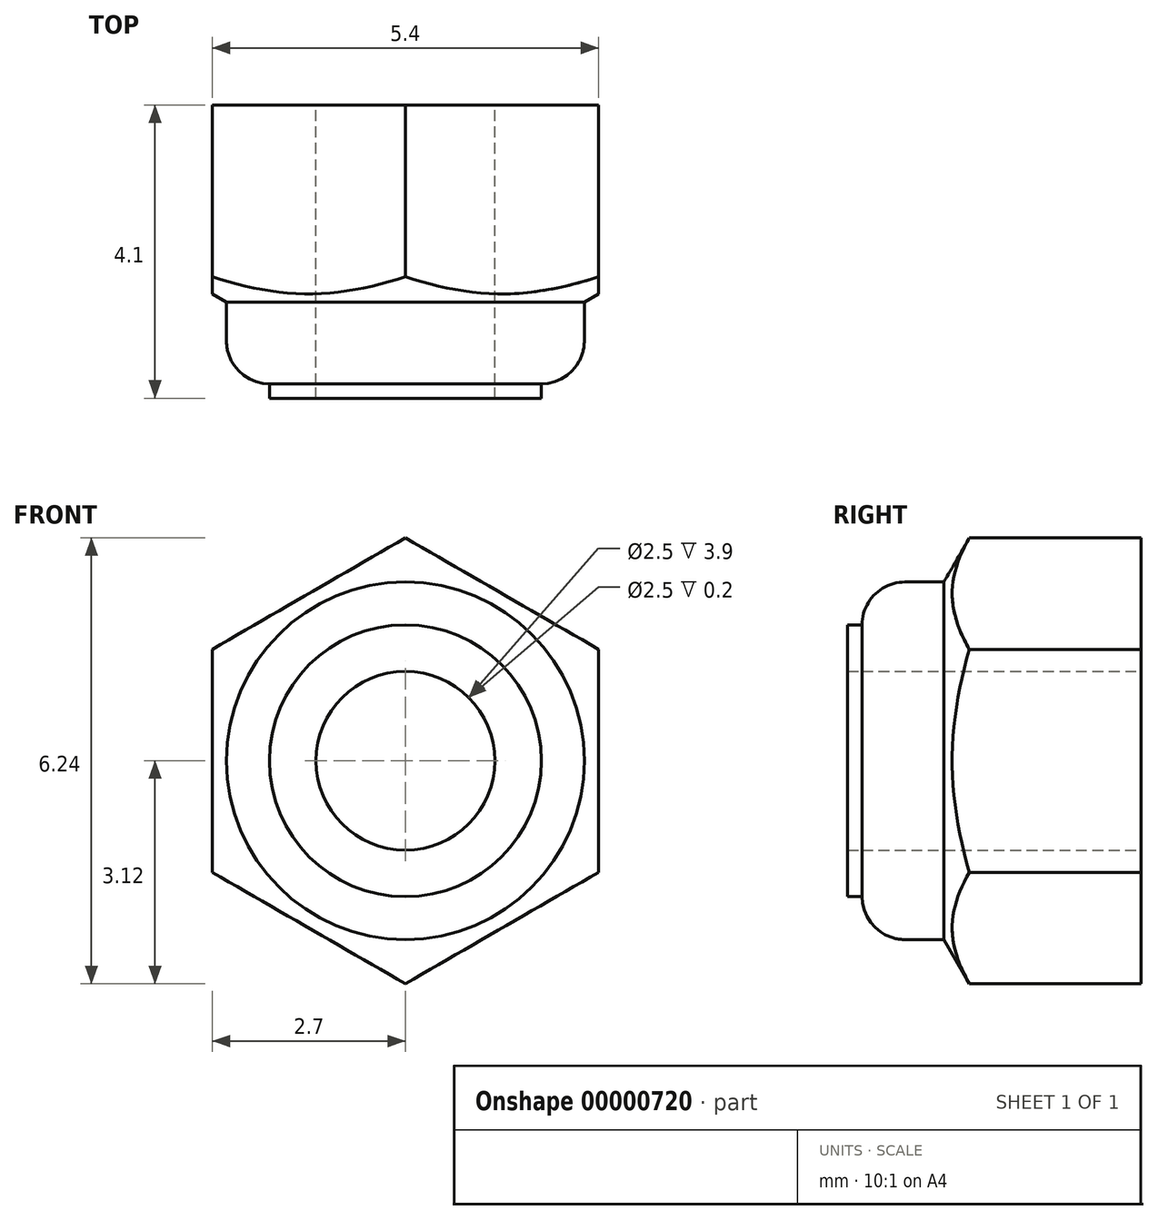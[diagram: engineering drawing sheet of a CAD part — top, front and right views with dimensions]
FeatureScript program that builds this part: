
annotation { "Feature Type Name" : "Feature", "Feature Type Description" : "" }
export const myFeature = defineFeature(function(context is Context, id is Id, definition is map)
    precondition{}
    {
        {
            var Q0;
            Q0=qCreatedBy(makeId("Front.planeOp"),FACE);
            var sketch = newSketch(context, id + "F0", { "sketchPlane" : qUnion([Q0])});
            skCircle(sketch, "E0.cCircle", {"center": v(0, 0) * mm, "radius": 2.7 * mm, "construction": true});
            skLineSegment(sketch, "E0.0", {"start": v(2.7, 1.56) * mm, "end": v(2.7, -1.56) * mm});
            skLineSegment(sketch, "E0.1", {"start": v(2.7, -1.56) * mm, "end": v(0, -3.12) * mm});
            skLineSegment(sketch, "E0.2", {"start": v(0, -3.12) * mm, "end": v(-2.7, -1.56) * mm});
            skLineSegment(sketch, "E0.3", {"start": v(-2.7, -1.56) * mm, "end": v(-2.7, 1.56) * mm});
            skLineSegment(sketch, "E0.4", {"start": v(-2.7, 1.56) * mm, "end": v(0, 3.12) * mm});
            skLineSegment(sketch, "E0.5", {"start": v(0, 3.12) * mm, "end": v(2.7, 1.56) * mm});
            skPoint(sketch, "E0.0.midPoint", {"position": v(2.7, 0) * mm});
            skSolve(sketch);
        }
        {
            var Q0;
            Q0=makeQuery(id+"F0.imprint","IMPRINT",FACE,{"disambiguationData":[TD([[makeQuery(id+"F0.imprint","IMPRINT",EDGE,{"derivedFrom":sQuery(id+"F0.wireOp",EDGE,"E0.0")}),-1.0]])]});
            extrude(context, id + "F1", {"entities" : qUnion([Q0]), "depth" : 3 * mm});
        }
        {
            var Q0;
            Q0=qCreatedBy(makeId("Right.planeOp"),FACE);
            var sketch = newSketch(context, id + "F2", { "sketchPlane" : qUnion([Q0])});
            skLineSegment(sketch, "E1", {"start": v(-2.4, 3.12) * mm, "end": v(-4.2, 0) * mm});
            skLineSegment(sketch, "E2", {"start": v(-4.2, 0) * mm, "end": v(-12.28, 0) * mm});
            skLineSegment(sketch, "E3", {"start": v(-12.28, 0) * mm, "end": v(-12.28, 3.12) * mm});
            skLineSegment(sketch, "E4", {"start": v(-2.4, 3.12) * mm, "end": v(-12.28, 3.12) * mm});
            skLineSegment(sketch, "E5", {"start": v(-4.2, 0) * mm, "end": v(3.9, 0) * mm, "construction": true});
            skSolve(sketch);
        }
        {
            var Q0;
            Q0=makeQuery(id+"F2.imprint","IMPRINT",FACE,{"disambiguationData":[TD([[makeQuery(id+"F2.imprint","IMPRINT",EDGE,{"derivedFrom":sQuery(id+"F2.wireOp",EDGE,"E1")}),-1.0]])]});
            var Q1;
            Q1=sQuery(id+"F2.wireOp",EDGE,"E5");
            revolve(context, id + "F3", {"operationType" : NewBodyOperationType.REMOVE, "entities" : qUnion([Q0]), "axis" : qUnion([Q1]), "revolveType" : RevolveType.FULL, "oppositeDirection" : true});
        }
        {
            var Q0;
            Q0=makeQuery(id+"F1.opExtrude","CAP_FACE",FACE,{"disambiguationData":[OSD([sQuery(id+"F0.wireOp",EDGE,"E0.0"),sQuery(id+"F0.wireOp",EDGE,"E0.1"),sQuery(id+"F0.wireOp",EDGE,"E0.2"),sQuery(id+"F0.wireOp",EDGE,"E0.3"),sQuery(id+"F0.wireOp",EDGE,"E0.4"),sQuery(id+"F0.wireOp",EDGE,"E0.5")])],"isStart":true});
            var sketch = newSketch(context, id + "F4", { "sketchPlane" : qUnion([Q0])});
            skCircle(sketch, "E6", {"center": v(0, 0) * mm, "radius": 2.5 * mm});
            skSolve(sketch);
        }
        {
            var Q0;
            Q0=makeQuery(id+"F4.imprint","IMPRINT",FACE,{"disambiguationData":[TD([[makeQuery(id+"F4.imprint","IMPRINT",EDGE,{"derivedFrom":sQuery(id+"F4.wireOp",EDGE,"E6")}),1.0]])]});
            extrude(context, id + "F5", {"entities" : qUnion([Q0]), "operationType" : NewBodyOperationType.ADD, "oppositeDirection" : true, "depth" : 3.9 * mm});
        }
        {
            var Q0;
            Q0=makeQuery(id+"F5.opExtrude","CAP_EDGE",EDGE,{"disambiguationData":[OSD([sQuery(id+"F4.wireOp",EDGE,"E6")])],"isStart":false});
            fillet(context, id + "F6", {"entities" : qUnion([Q0]), "radius" : .6 * mm, "tangentPropagation" : true, "allowEdgeOverflow" : false});
        }
        {
            var Q0;
            Q0=makeQuery(id+"F5.opExtrude","CAP_FACE",FACE,{"disambiguationData":[OSD([sQuery(id+"F4.wireOp",EDGE,"E6")])],"isStart":false});
            var sketch = newSketch(context, id + "F7", { "sketchPlane" : qUnion([Q0])});
            skCircle(sketch, "E7.0", {"center": v(0, 0) * mm, "radius": 1.9 * mm});
            skSolve(sketch);
        }
        {
            var Q0;
            Q0=makeQuery(id+"F7.imprint","IMPRINT",FACE,{"disambiguationData":[TD([[makeQuery(id+"F7.imprint","IMPRINT",EDGE,{"derivedFrom":sQuery(id+"F7.wireOp",EDGE,"E7.0")}),1.0]])]});
            extrude(context, id + "F8", {"entities" : qUnion([Q0]), "depth" : .2 * mm});
        }
        {
            var Q0;
            Q0=makeQuery(id+"F1.opExtrude","CAP_FACE",FACE,{"disambiguationData":[OSD([sQuery(id+"F0.wireOp",EDGE,"E0.0"),sQuery(id+"F0.wireOp",EDGE,"E0.1"),sQuery(id+"F0.wireOp",EDGE,"E0.2"),sQuery(id+"F0.wireOp",EDGE,"E0.3"),sQuery(id+"F0.wireOp",EDGE,"E0.4"),sQuery(id+"F0.wireOp",EDGE,"E0.5")])],"isStart":true});
            var sketch = newSketch(context, id + "F9", { "sketchPlane" : qUnion([Q0])});
            skCircle(sketch, "E8", {"center": v(0, 0) * mm, "radius": 1.25 * mm});
            skSolve(sketch);
        }
        {
            var Q0;
            Q0=makeQuery(id+"F9.imprint","IMPRINT",FACE,{"disambiguationData":[TD([[makeQuery(id+"F9.imprint","IMPRINT",EDGE,{"derivedFrom":sQuery(id+"F9.wireOp",EDGE,"E8")}),1.0]])]});
            extrude(context, id + "F10", {"entities" : qUnion([Q0]), "operationType" : NewBodyOperationType.REMOVE, "oppositeDirection" : true, "depth" : 25 * mm});
        }
    });
